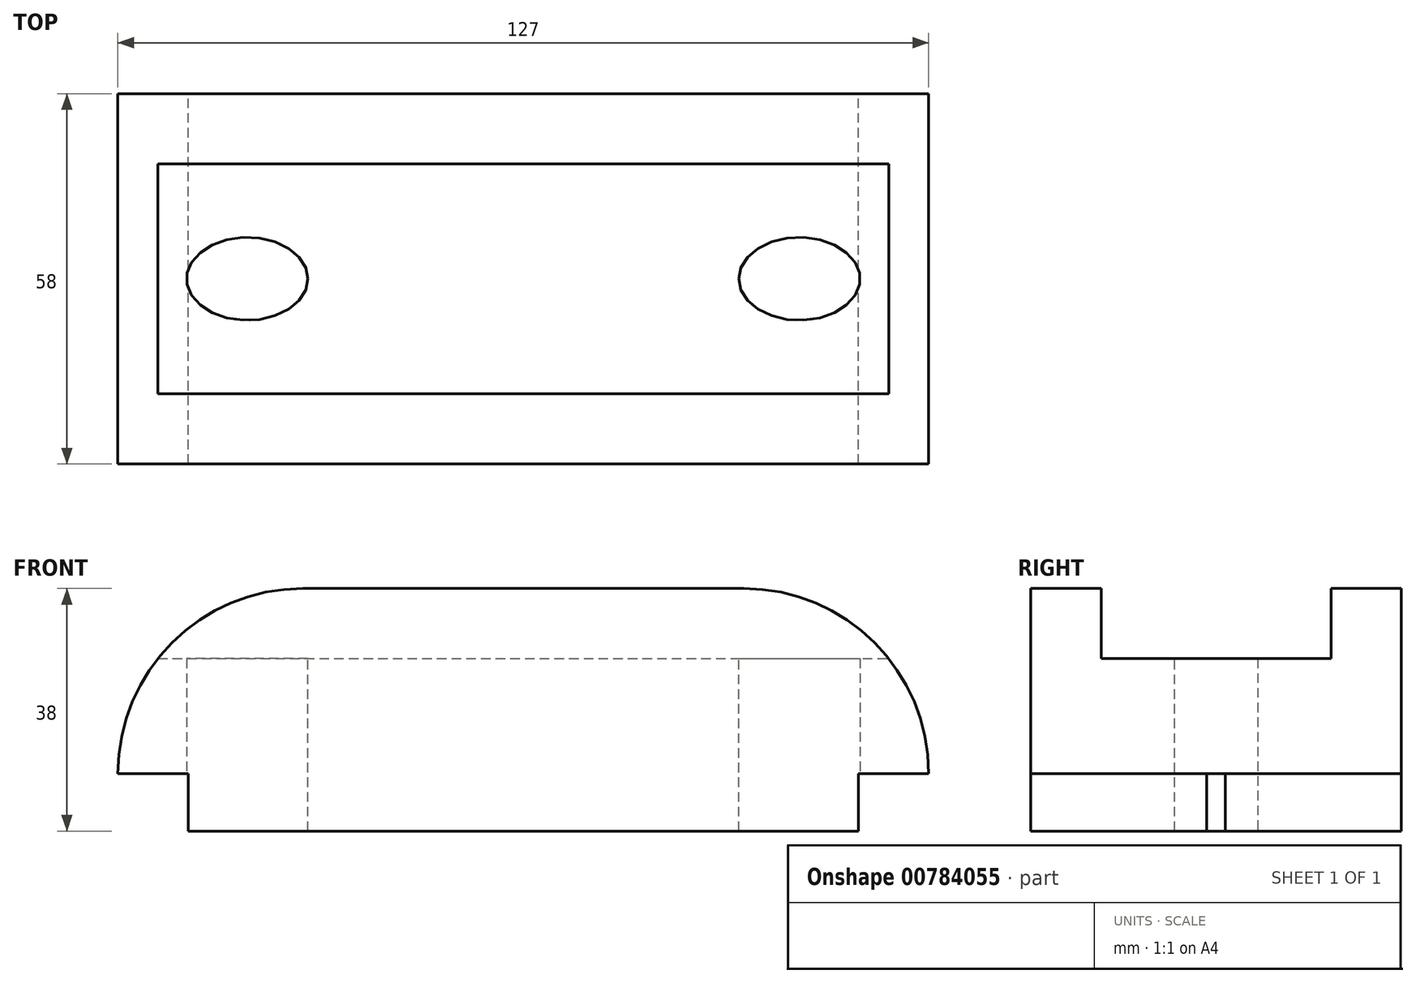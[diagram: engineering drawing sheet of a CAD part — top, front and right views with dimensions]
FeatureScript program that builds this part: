
annotation { "Feature Type Name" : "Feature", "Feature Type Description" : "" }
export const myFeature = defineFeature(function(context is Context, id is Id, definition is map)
    precondition{}
    {
        {
            var Q0;
            Q0=qCreatedBy(makeId("Right.planeOp"),FACE);
            var sketch = newSketch(context, id + "F0", { "sketchPlane" : qUnion([Q0])});
            skLineSegment(sketch, "E0.bottom", {"start": v(-60.84, 44.04) * mm, "end": v(-2.84, 44.04) * mm});
            skLineSegment(sketch, "E0.top", {"start": v(-60.84, 6.04) * mm, "end": v(-2.84, 6.04) * mm});
            skLineSegment(sketch, "E0.left", {"start": v(-60.84, 44.04) * mm, "end": v(-60.84, 6.04) * mm});
            skLineSegment(sketch, "E0.right", {"start": v(-2.84, 44.04) * mm, "end": v(-2.84, 6.04) * mm});
            skSolve(sketch);
        }
        {
            var Q0;
            Q0 = qSketchRegion(id + "F0", true);
            extrude(context, id + "F1", {"entities" : qUnion([Q0]), "depth" : 127 * mm, "offsetDistance" : 25.4 * mm});
        }
        {
            var Q0;
            Q0=makeQuery(id+"F1.opExtrude","CAP_FACE",FACE,{"disambiguationData":[OSD([sQuery(id+"F0.wireOp",EDGE,"E0.bottom"),sQuery(id+"F0.wireOp",EDGE,"E0.top"),sQuery(id+"F0.wireOp",EDGE,"E0.left"),sQuery(id+"F0.wireOp",EDGE,"E0.right")])],"isStart":false});
            var sketch = newSketch(context, id + "F2", { "sketchPlane" : qUnion([Q0])});
            skLineSegment(sketch, "E1", {"start": v(-60.84, 6.04) * mm, "end": v(-60.84, 15.04) * mm});
            skLineSegment(sketch, "E2", {"start": v(-2.84, 6.04) * mm, "end": v(-2.84, 15.04) * mm});
            skLineSegment(sketch, "E3", {"start": v(-60.84, 15.04) * mm, "end": v(-2.84, 15.04) * mm});
            skSolve(sketch);
        }
        {
            var Q0;
            Q0=makeQuery(id+"F2.imprint","IMPRINT",FACE,{"disambiguationData":[TD([[makeQuery(id+"F2.imprint","IMPRINT",EDGE,{"derivedFrom":sQuery(id+"F2.wireOp",EDGE,"E1")}),1.0]])]});
            extrude(context, id + "F3", {"entities" : qUnion([Q0]), "operationType" : NewBodyOperationType.REMOVE, "oppositeDirection" : true, "depth" : 11 * mm, "offsetDistance" : 25.4 * mm});
        }
        {
            var Q0;
            Q0=makeQuery(id+"F1.opExtrude","CAP_FACE",FACE,{"disambiguationData":[OSD([sQuery(id+"F0.wireOp",EDGE,"E0.bottom"),sQuery(id+"F0.wireOp",EDGE,"E0.top"),sQuery(id+"F0.wireOp",EDGE,"E0.left"),sQuery(id+"F0.wireOp",EDGE,"E0.right")])],"isStart":true});
            var sketch = newSketch(context, id + "F4", { "sketchPlane" : qUnion([Q0])});
            skLineSegment(sketch, "E4", {"start": v(2.84, 6.04) * mm, "end": v(2.84, 15.04) * mm});
            skLineSegment(sketch, "E5", {"start": v(2.84, 15.04) * mm, "end": v(60.84, 15.04) * mm});
            skLineSegment(sketch, "E6", {"start": v(60.84, 15.04) * mm, "end": v(60.84, 6.04) * mm});
            skSolve(sketch);
        }
        {
            var Q0;
            Q0=makeQuery(id+"F4.imprint","IMPRINT",FACE,{"disambiguationData":[TD([[makeQuery(id+"F4.imprint","IMPRINT",EDGE,{"derivedFrom":sQuery(id+"F4.wireOp",EDGE,"E4")}),1.0]])]});
            extrude(context, id + "F5", {"entities" : qUnion([Q0]), "operationType" : NewBodyOperationType.REMOVE, "oppositeDirection" : true, "depth" : 11 * mm, "offsetDistance" : 25.4 * mm});
        }
        {
            var Q0;
            Q0=makeQuery(id+"F1.opExtrude","SWEPT_FACE",FACE,{"disambiguationData":[OSD([sQuery(id+"F0.wireOp",EDGE,"E0.bottom")])]});
            var sketch = newSketch(context, id + "F6", { "sketchPlane" : qUnion([Q0])});
            skLineSegment(sketch, "E7", {"start": v(0, -2.84) * mm, "end": v(0, -13.84) * mm});
            skLineSegment(sketch, "E8", {"start": v(0, -13.84) * mm, "end": v(0, -49.84) * mm});
            skLineSegment(sketch, "E9", {"start": v(0, -49.84) * mm, "end": v(0, -60.84) * mm});
            skLineSegment(sketch, "E10", {"start": v(0, -13.84) * mm, "end": v(127, -13.84) * mm});
            skLineSegment(sketch, "E11", {"start": v(0, -49.84) * mm, "end": v(127, -49.84) * mm});
            skLineSegment(sketch, "E12", {"start": v(0, -2.84) * mm, "end": v(127, -2.84) * mm});
            skLineSegment(sketch, "E13", {"start": v(0, -60.84) * mm, "end": v(127, -60.84) * mm});
            skSolve(sketch);
        }
        {
            var Q0;
            Q0=makeQuery(id+"F6.imprint","IMPRINT",FACE,{"disambiguationData":[TD([[makeQuery(id+"F6.imprint","IMPRINT",EDGE,{"derivedFrom":sQuery(id+"F6.wireOp",EDGE,"E8")}),-1.0]])]});
            extrude(context, id + "F7", {"entities" : qUnion([Q0]), "operationType" : NewBodyOperationType.REMOVE, "oppositeDirection" : true, "depth" : 11 * mm, "offsetDistance" : 25.4 * mm});
        }
        {
            var Q0;
            {var subQ0=sQuery(id+"F0.wireOp",EDGE,"E0.bottom");var subQ1=sQuery(id+"F0.wireOp",EDGE,"E0.left");Q0=makeQuery(id+"F7.boolean.opBoolean","SPLIT",EDGE,{"disambiguationData":[TD([makeQuery(id+"F1.opExtrude","SWEPT_FACE",FACE,{"disambiguationData":[OSD([subQ1])]})])],"derivedFrom":makeQuery(id+"F1.opExtrude","CAP_EDGE",EDGE,{"disambiguationData":[OSD([subQ0])],"isStart":false})});}
            var Q1;
            {var subQ0=sQuery(id+"F0.wireOp",EDGE,"E0.bottom");var subQ1=sQuery(id+"F0.wireOp",EDGE,"E0.right");Q1=makeQuery(id+"F7.boolean.opBoolean","SPLIT",EDGE,{"disambiguationData":[TD([makeQuery(id+"F1.opExtrude","SWEPT_FACE",FACE,{"disambiguationData":[OSD([subQ1])]})])],"derivedFrom":makeQuery(id+"F1.opExtrude","CAP_EDGE",EDGE,{"disambiguationData":[OSD([subQ0])],"isStart":false})});}
            var Q2;
            {var subQ0=sQuery(id+"F0.wireOp",EDGE,"E0.bottom");var subQ1=sQuery(id+"F0.wireOp",EDGE,"E0.right");Q2=makeQuery(id+"F7.boolean.opBoolean","SPLIT",EDGE,{"disambiguationData":[TD([makeQuery(id+"F1.opExtrude","SWEPT_FACE",FACE,{"disambiguationData":[OSD([subQ1])]})])],"derivedFrom":makeQuery(id+"F1.opExtrude","CAP_EDGE",EDGE,{"disambiguationData":[OSD([subQ0])],"isStart":true})});}
            var Q3;
            {var subQ0=sQuery(id+"F0.wireOp",EDGE,"E0.bottom");var subQ1=sQuery(id+"F0.wireOp",EDGE,"E0.left");Q3=makeQuery(id+"F7.boolean.opBoolean","SPLIT",EDGE,{"disambiguationData":[TD([makeQuery(id+"F1.opExtrude","SWEPT_FACE",FACE,{"disambiguationData":[OSD([subQ1])]})])],"derivedFrom":makeQuery(id+"F1.opExtrude","CAP_EDGE",EDGE,{"disambiguationData":[OSD([subQ0])],"isStart":true})});}
            fillet(context, id + "F8", {"entities" : qUnion([Q0, Q1, Q2, Q3]), "radius" : 29 * mm, "tangentPropagation" : true, "allowEdgeOverflow" : false});
        }
        {
            var Q0;
            Q0=makeQuery(id+"F7.boolean.opBoolean","COPY",FACE,{"derivedFrom":makeQuery(id+"F7.opExtrude","CAP_FACE",FACE,{"disambiguationData":[OSD([sQuery(id+"F0.wireOp",EDGE,"E0.bottom"),sQuery(id+"F6.wireOp",EDGE,"E8"),sQuery(id+"F6.wireOp",EDGE,"E10"),sQuery(id+"F6.wireOp",EDGE,"E11")])],"isStart":false})});
            var sketch = newSketch(context, id + "F9", { "sketchPlane" : qUnion([Q0])});
            skSolve(sketch);
        }
        {
            var Q0;
            {var subQ0=sQuery(id+"F6.wireOp",EDGE,"E10");Q0=makeQuery(id+"F9.imprint","IMPRINT",FACE,{"disambiguationData":[TD([[makeQuery(id+"F9.imprint","IMPRINT",EDGE,{"derivedFrom":makeQuery(id+"F7.boolean.opBoolean","COPY",EDGE,{"derivedFrom":makeQuery(id+"F7.opExtrude","CAP_EDGE",EDGE,{"disambiguationData":[OSD([subQ0])],"isStart":false})})}),-1.0]])]});}
            var sketch = newSketch(context, id + "F10", { "sketchPlane" : qUnion([Q0])});
            skSolve(sketch);
        }
        {
            var Q0;
            {var subQ0=sQuery(id+"F6.wireOp",EDGE,"E10");Q0=makeQuery(id+"F10.imprint","IMPRINT",FACE,{"disambiguationData":[TD([[makeQuery(id+"F10.imprint","IMPRINT",EDGE,{"derivedFrom":makeQuery(id+"F9.imprint","IMPRINT",EDGE,{"derivedFrom":makeQuery(id+"F7.boolean.opBoolean","COPY",EDGE,{"derivedFrom":makeQuery(id+"F7.opExtrude","CAP_EDGE",EDGE,{"disambiguationData":[OSD([subQ0])],"isStart":false})})})}),-1.0]])]});}
            var sketch = newSketch(context, id + "F11", { "sketchPlane" : qUnion([Q0])});
            skEllipse(sketch, "E14", {"center": v(20.26, -31.84) * mm, "majorRadius": 9.5 * mm, "minorRadius": 6.5 * mm, "majorAxis": v(1, 0)});
            skEllipse(sketch, "E15", {"center": v(106.74, -31.84) * mm, "majorRadius": 9.5 * mm, "minorRadius": 6.5 * mm, "majorAxis": v(-1, 0)});
            skSolve(sketch);
        }
        {
            var Q0;
            Q0 = qSketchRegion(id + "F11", true);
            extrude(context, id + "F12", {"entities" : qUnion([Q0]), "operationType" : NewBodyOperationType.REMOVE, "oppositeDirection" : true, "depth" : 38 * mm, "offsetDistance" : 25.4 * mm});
        }
    });
